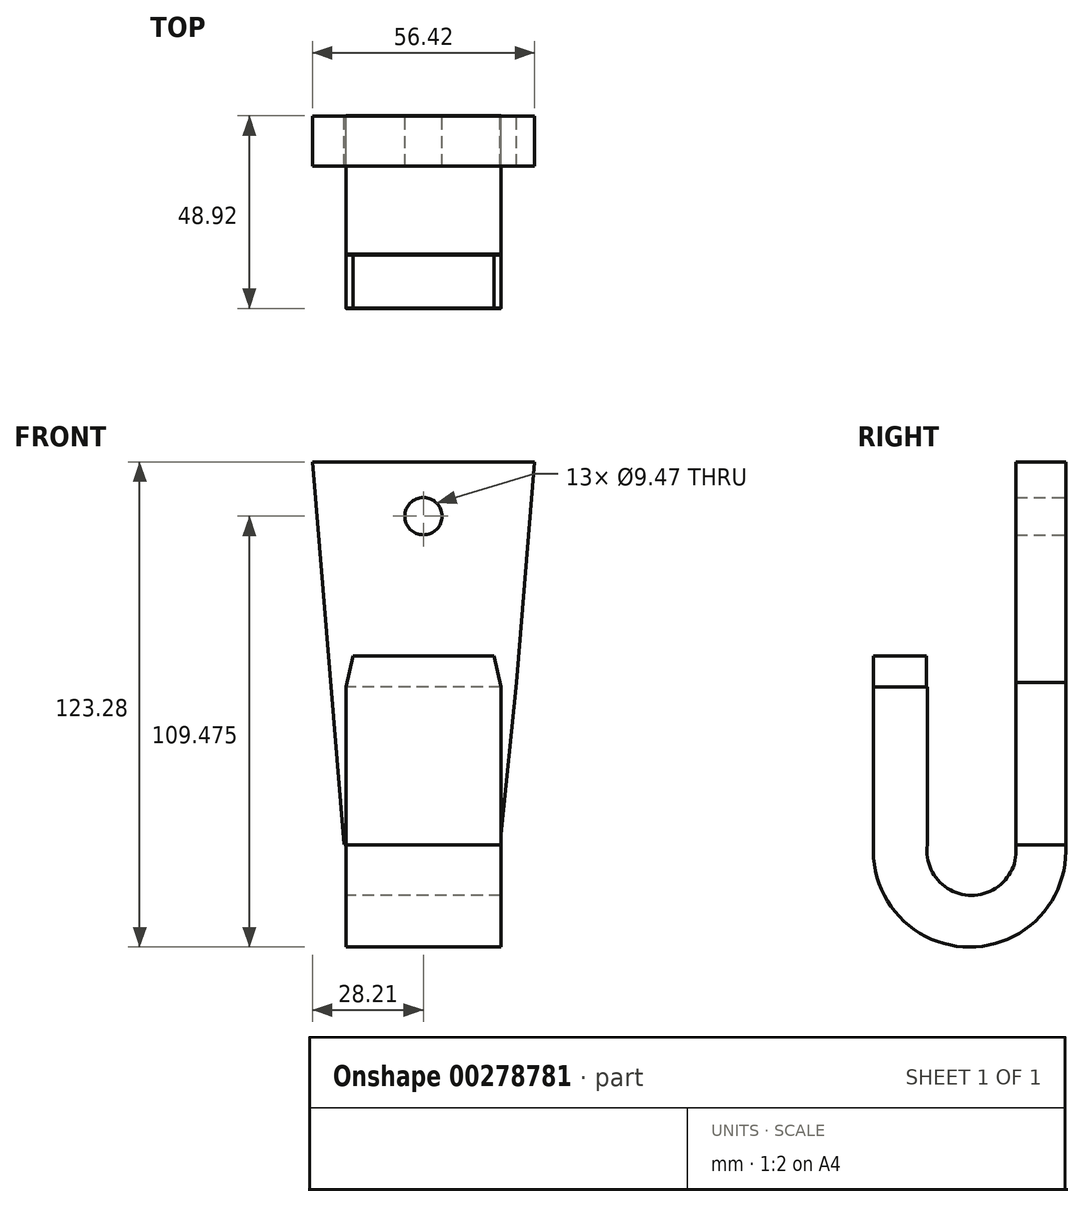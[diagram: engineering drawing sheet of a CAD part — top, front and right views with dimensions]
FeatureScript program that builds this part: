
annotation { "Feature Type Name" : "Feature", "Feature Type Description" : "" }
export const myFeature = defineFeature(function(context is Context, id is Id, definition is map)
    precondition{}
    {
        {
            var Q0;
            Q0=qCreatedBy(makeId("Front.planeOp"),FACE);
            var sketch = newSketch(context, id + "F0", { "sketchPlane" : qUnion([Q0])});
            skLineSegment(sketch, "E0", {"start": v(-28.2, 56.04) * mm, "end": v(28.2, 56.04) * mm});
            skLineSegment(sketch, "E1", {"start": v(28.2, 56.04) * mm, "end": v(23.6, 0) * mm});
            skLineSegment(sketch, "E2.MirrorCS", {"start": v(-28.2, 56.04) * mm, "end": v(-23.6, 0) * mm});
            skLineSegment(sketch, "E3.MirrorCS", {"start": v(28.2, 56.04) * mm, "end": v(-28.2, 56.04) * mm});
            skPoint(sketch, "E4.orphan", {"position": v(-33, 56.04) * mm});
            skPoint(sketch, "E5.orphan", {"position": v(33, 56.04) * mm});
            skLineSegment(sketch, "E6", {"start": v(-23.6, 0) * mm, "end": v(-20.2, -41.22) * mm});
            skLineSegment(sketch, "E7", {"start": v(23.6, 0) * mm, "end": v(19.42, -41.25) * mm});
            skLineSegment(sketch, "E8", {"start": v(-20.2, -41.22) * mm, "end": v(19.42, -41.25) * mm});
            skCircle(sketch, "E9", {"center": v(0, 42.23) * mm, "radius": 4.73 * mm});
            skSolve(sketch);
        }
        {
            var Q0;
            Q0=makeQuery(id+"F0.imprint","IMPRINT",FACE,{"disambiguationData":[TD([[makeQuery(id+"F0.imprint","IMPRINT",EDGE,{"derivedFrom":sQuery(id+"F0.wireOp",EDGE,"E1")}),-1.0]])]});
            extrude(context, id + "F1", {"entities" : qUnion([Q0]), "depth" : 12.7 * mm});
        }
        {
            var Q0;
            Q0=qCreatedBy(makeId("Right.planeOp"),FACE);
            var sketch = newSketch(context, id + "F2", { "sketchPlane" : qUnion([Q0])});
            skLineSegment(sketch, "E10", {"start": v(-29.29, -31.32) * mm, "end": v(-29.29, -31.46) * mm});
            skPoint(sketch, "E11.orphan", {"position": v(-39.48, -31.46) * mm});
            skLineSegment(sketch, "E12", {"start": v(-12.7, -38.25) * mm, "end": v(-12.7, -41.22) * mm});
            skLineSegment(sketch, "E13", {"start": v(-12.7, -41.22) * mm, "end": v(-12.7, -41.26) * mm});
            skLineSegment(sketch, "E14", {"start": v(-12.7, -41.26) * mm, "end": v(-9.94, -41.26) * mm});
            skLineSegment(sketch, "E15", {"start": v(-9.94, -41.26) * mm, "end": v(0, -41.25) * mm});
            skArc(sketch, "E16", {"start": v(0, -41.25) * mm, "mid": v(-24.4, -67.24) * mm, "end": v(-48.82, -41.25) * mm});
            skLineSegment(sketch, "E17", {"start": v(-48.82, -41.25) * mm, "end": v(-48.82, -1.1) * mm});
            skLineSegment(sketch, "E18", {"start": v(-48.82, -1.1) * mm, "end": v(-36.47, -1.1) * mm});
            skArc(sketch, "E19", {"start": v(-12.7, -41.22) * mm, "mid": v(-23.91, -54.1) * mm, "end": v(-35.12, -41.22) * mm});
            skLineSegment(sketch, "E20", {"start": v(-35.12, -41.22) * mm, "end": v(-35.12, -1.1) * mm});
            skLineSegment(sketch, "E21", {"start": v(-35.12, -1.1) * mm, "end": v(-36.47, -1.1) * mm});
            skSolve(sketch);
        }
        {
            var Q0;
            {var subQ0=sQuery(id+"F2.wireOp",EDGE,"E15");Q0=makeQuery(id+"F2.imprint","IMPRINT",FACE,{"disambiguationData":[TD([[makeQuery(id+"F2.imprint","IMPRINT",EDGE,{"derivedFrom":subQ0}),-1.0]])]});}
            extrude(context, id + "F3", {"entities" : qUnion([Q0]), "endBound" : BoundingType.SYMMETRIC, "depth" : 39.37 * mm});
        }
        {
            var Q0;
            Q0=makeQuery(id+"F3.opExtrude","SWEPT_FACE",FACE,{"disambiguationData":[OSD([sQuery(id+"F2.wireOp",EDGE,"E17")])]});
            var sketch = newSketch(context, id + "F4", { "sketchPlane" : qUnion([Q0])});
            skLineSegment(sketch, "E22", {"start": v(-19.69, -1.1) * mm, "end": v(-17.9, 6.78) * mm});
            skLineSegment(sketch, "E23", {"start": v(-17.9, 6.78) * mm, "end": v(0, 6.78) * mm});
            skLineSegment(sketch, "E24.MirrorCS", {"start": v(17.9, 6.78) * mm, "end": v(0, 6.78) * mm});
            skLineSegment(sketch, "E25.MirrorCS", {"start": v(19.69, -1.1) * mm, "end": v(17.9, 6.78) * mm});
            skSolve(sketch);
        }
        {
            var Q0;
            Q0=makeQuery(id+"F4.imprint","IMPRINT",FACE,{"disambiguationData":[TD([[makeQuery(id+"F4.imprint","IMPRINT",EDGE,{"derivedFrom":sQuery(id+"F4.wireOp",EDGE,"E22")}),-1.0]])]});
            extrude(context, id + "F5", {"entities" : qUnion([Q0]), "operationType" : NewBodyOperationType.ADD, "oppositeDirection" : true, "depth" : 13.46 * mm});
        }
    });
